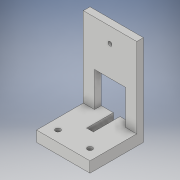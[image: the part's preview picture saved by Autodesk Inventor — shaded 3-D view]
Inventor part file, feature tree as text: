
AUTODESK INVENTOR PART (.ipt)
format: ipt  version: 2017 (Build 210142000, 142)  size: 189,952 bytes
history: native  units: in
note: dims shown in document units (in); Inventor stores cm internally (conversion verified against a paired STEP export)
features: extrude x7, sketch x7
ambient origin geometry x8: Origin, YZ Plane, XZ Plane, XY Plane, X Axis, Y Axis, Z Axis, Center Point
bodies: Solid1 (feature_tree)
feature tree (14):
  extrude  "Extrusion1"  Depth=2.0in
  extrude  "Extrusion2"  TaperAngle=0.0deg  [1 undecoded]
  extrude  "Extrusion3"  Depth=2.0in
  extrude  "Extrusion5"  Depth=1.3in
  extrude  "Extrusion6"  TaperAngle=0.0deg  [1 undecoded]
  extrude  "Extrusion7"  Depth=0.6in
  extrude  "Extrusion8"  Depth=1.0in
  sketch  "Sketch1"  dims[d1=0.4in d2=2.0in]
  sketch  "Sketch2"  dims[d3=2.0in d4=0.0in d6=0.0in]
  sketch  "Sketch3"  dims[d7=2.0in d9=0.58in]
  sketch  "Sketch5"  dims[d10=0.58in d11=1.3in]
  sketch  "Sketch6"  dims[d12=0.25in d13=0.0in d15=0.0in]
  sketch  "Sketch8"  dims[d16=2.025in d17=0.6in]
  sketch  "Sketch9"  dims[d18=0.0in d19=0.57in d20=0.25in d21=0.0in d26=0.9683in d27=1.0125in d28=0.6in d29=0.445in d30=0.15in d31=1.0in d32=0.0in d33=0.57in d34=0.25in d35=0.0in d36=0.1875in d37=0.1875in d38=0.4in d39=0.4in d40=0.4in d41=0.4in d42=1.0in d43=0.0in d45=0.25in d46=0.125in d47=1.0in d48=0.0in]
note: 2 required parameter values undecoded (feature->parameter linkage not recoverable at this tier; creation-order binding heuristic only, values carry confidence <= 0.55)
